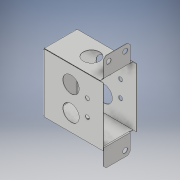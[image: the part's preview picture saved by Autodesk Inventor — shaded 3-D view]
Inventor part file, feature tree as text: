
AUTODESK INVENTOR PART (.ipt)
format: ipt  version: 2019 (Build 230136000, 136)  size: 603,648 bytes
history: native  units: mm
features: other x9, sketch x7
ambient origin geometry x8: Origin, YZ Plane, XZ Plane, XY Plane, X Axis, Y Axis, Z Axis, Center Point
bodies: Body1 (feature_tree)
feature tree (16):
  other  "Sólido1"
  other  "Cara1"
  other  "Pliegue2"
  other  "Pliegue3"
  other  "Pliegue4"
  other  "Pliegue5"
  other  "Pliegue6"
  other  "Pliegue7"
  sketch  "Boceto1"  dims[d0=71.58mm]
  other  "Placa1"
  sketch  "Boceto2"  dims[d10=71.58mm]
  sketch  "Boceto3"  dims[d11=71.58mm]
  sketch  "Boceto4"  dims[d12=20.0mm]
  sketch  "Boceto5"  dims[d13=20.0mm]
  sketch  "Boceto6"  dims[d14=5.0mm]
  sketch  "Boceto7"  dims[d15=5.0mm d16=5.0mm d17=5.0mm d18=39.25mm d19=39.25mm d20=30.0mm d21=20.0mm d23=20.0mm d24=20.0mm d25=28.198359mm d28=4.0mm d29=4.0mm d34=20.16mm d35=20.16mm d36=4.0mm d37=135.0deg d38=4.0mm d39=20.0mm d40=6.0mm d43=6.0mm d44=6.0mm d45=0.5mm d52=0.5mm d53=0.25mm d54=1.0mm d55=0.5mm d56=90.0deg d57=0.5mm d58=0.5mm d59=0.25mm d60=1.0mm d61=0.5mm d62=90.0deg d63=0.5mm d64=0.5mm d65=0.25mm d66=1.0mm d67=0.5mm d68=90.0deg d69=0.5mm d70=0.5mm d71=0.25mm d72=1.0mm d73=0.5mm d74=90.0deg d75=0.5mm d76=0.5mm d77=0.25mm d78=1.0mm d79=0.5mm d80=90.0deg d81=0.5mm d82=0.5mm d83=0.25mm d84=1.0mm d85=0.5mm d86=90.0deg d87=0.5mm]
